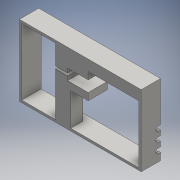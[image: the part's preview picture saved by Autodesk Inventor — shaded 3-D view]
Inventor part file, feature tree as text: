
AUTODESK INVENTOR PART (.ipt)
format: ipt  version: 2016 (Build 200138000, 138)  size: 174,080 bytes
history: native  units: mm
features: sketch x3, extrude x3, fillet x1
ambient origin geometry x8: Origin, YZ Plane, XZ Plane, XY Plane, X Axis, Y Axis, Z Axis, Center Point
bodies: Body1 (feature_tree)
feature tree (7):
  sketch  "Sketch1"  dims[d2=2.5mm d3=10.0mm]
  extrude  "Extrusion5"  Depth=10.0mm
  extrude  "Extrusion6"  Depth=21.0mm
  extrude  "Extrusion7"  Depth=28.0mm
  fillet  "Fillet1"  Radius=55.0mm
  sketch  "Sketch2"  dims[d4=2.0mm d5=21.0mm]
  sketch  "Sketch3"  dims[d6=42.0mm d9=28.0mm d10=55.0mm d13=10.0mm d14=9.0mm d15=17.0mm d16=2.0mm d17=2.0mm d20=2.0mm d24=10.0mm d25=0.0mm d26=16.0mm d27=0.0mm d28=101.0mm d29=59.0mm d30=4.0mm d31=4.0mm d32=0.0mm d33=2.0mm d34=42.0mm d35=27.0mm d36=56.5mm d37=12.5mm]
